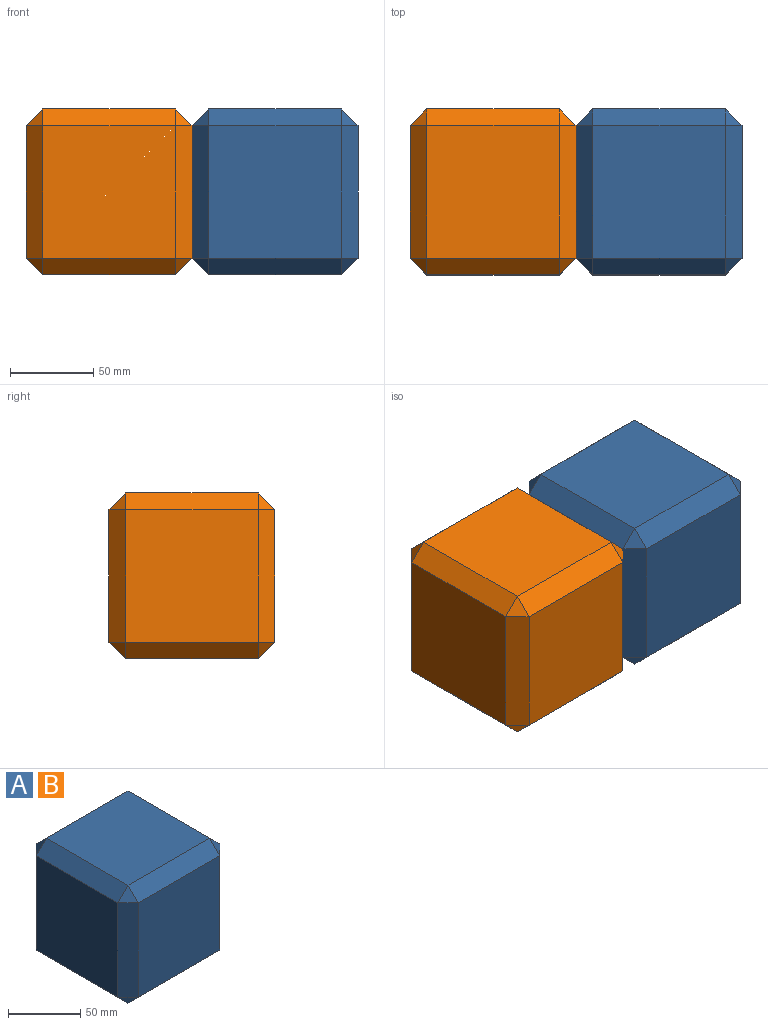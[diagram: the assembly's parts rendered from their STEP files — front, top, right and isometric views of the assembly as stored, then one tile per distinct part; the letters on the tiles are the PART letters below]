
ASSEMBLY  parts=2 mates=1
PART A: 26 faces, bbox 100x100x100 mm
  f0: plane 80x80mm, normal (0,-1,0), area 6400mm2, adj f6,f10,f11,f12
  f1: plane 80x80mm, normal (1,0,0), area 6400mm2, adj f6,f9,f13,f14
  f2: plane 80x80mm, normal (0,1,0), area 6400mm2, adj f14,f19,f22,f25
  f3: plane 80x80mm, normal (-1,0,0), area 6400mm2, adj f11,f20,f21,f25
  f4: plane 80x80mm, normal (0,0,1), area 6400mm2, adj f9,f10,f19,f20
  f5: plane 80x80mm, normal (0,0,-1), area 6400mm2, adj f12,f13,f21,f22
  f6: plane 80x10mm, normal (0.71,-0.71,0), area 1131.4mm2, adj f0,f1,f7,f8
  f7: plane 10x10mm, normal (0.58,-0.58,0.58), area 86.6mm2, adj f6,f9,f10
  f8: plane 10x10mm, normal (0.58,-0.58,-0.58), area 86.6mm2, adj f6,f12,f13
  f9: plane 80x10mm, normal (0.71,0,0.71), area 1131.4mm2, adj f1,f4,f7,f15
  f10: plane 80x10mm, normal (0,-0.71,0.71), area 1131.4mm2, adj f0,f4,f7,f16
  f11: plane 80x10mm, normal (-0.71,-0.71,0), area 1131.4mm2, adj f0,f3,f16,f17
  f12: plane 80x10mm, normal (0,-0.71,-0.71), area 1131.4mm2, adj f0,f5,f8,f17
  f13: plane 80x10mm, normal (0.71,0,-0.71), area 1131.4mm2, adj f1,f5,f8,f18
  f14: plane 80x10mm, normal (0.71,0.71,0), area 1131.4mm2, adj f1,f2,f15,f18
  f15: plane 10x10mm, normal (0.58,0.58,0.58), area 86.6mm2, adj f9,f14,f19
  f16: plane 10x10mm, normal (-0.58,-0.58,0.58), area 86.6mm2, adj f10,f11,f20
  f17: plane 10x10mm, normal (-0.58,-0.58,-0.58), area 86.6mm2, adj f11,f12,f21
  f18: plane 10x10mm, normal (0.58,0.58,-0.58), area 86.6mm2, adj f13,f14,f22
  f19: plane 80x10mm, normal (0,0.71,0.71), area 1131.4mm2, adj f2,f4,f15,f23
  f20: plane 80x10mm, normal (-0.71,0,0.71), area 1131.4mm2, adj f3,f4,f16,f23
  f21: plane 80x10mm, normal (-0.71,0,-0.71), area 1131.4mm2, adj f3,f5,f17,f24
  f22: plane 80x10mm, normal (0,0.71,-0.71), area 1131.4mm2, adj f2,f5,f18,f24
  f23: plane 10x10mm, normal (-0.58,0.58,0.58), area 86.6mm2, adj f19,f20,f25
  f24: plane 10x10mm, normal (-0.58,0.58,-0.58), area 86.6mm2, adj f21,f22,f25
  f25: plane 80x10mm, normal (-0.71,0.71,0), area 1131.4mm2, adj f2,f3,f23,f24
PART B: same geometry as A
PLACE A rot(axis=(0,1,0),180deg) t=(23.07,10.62,-46.2)mm
PLACE B t=(-76.93,10.62,-46.2)mm
MATE fastened A.f1 <-> B.f1  axis (-1,0,0) through (-26.93,10.62,-46.2)mm
